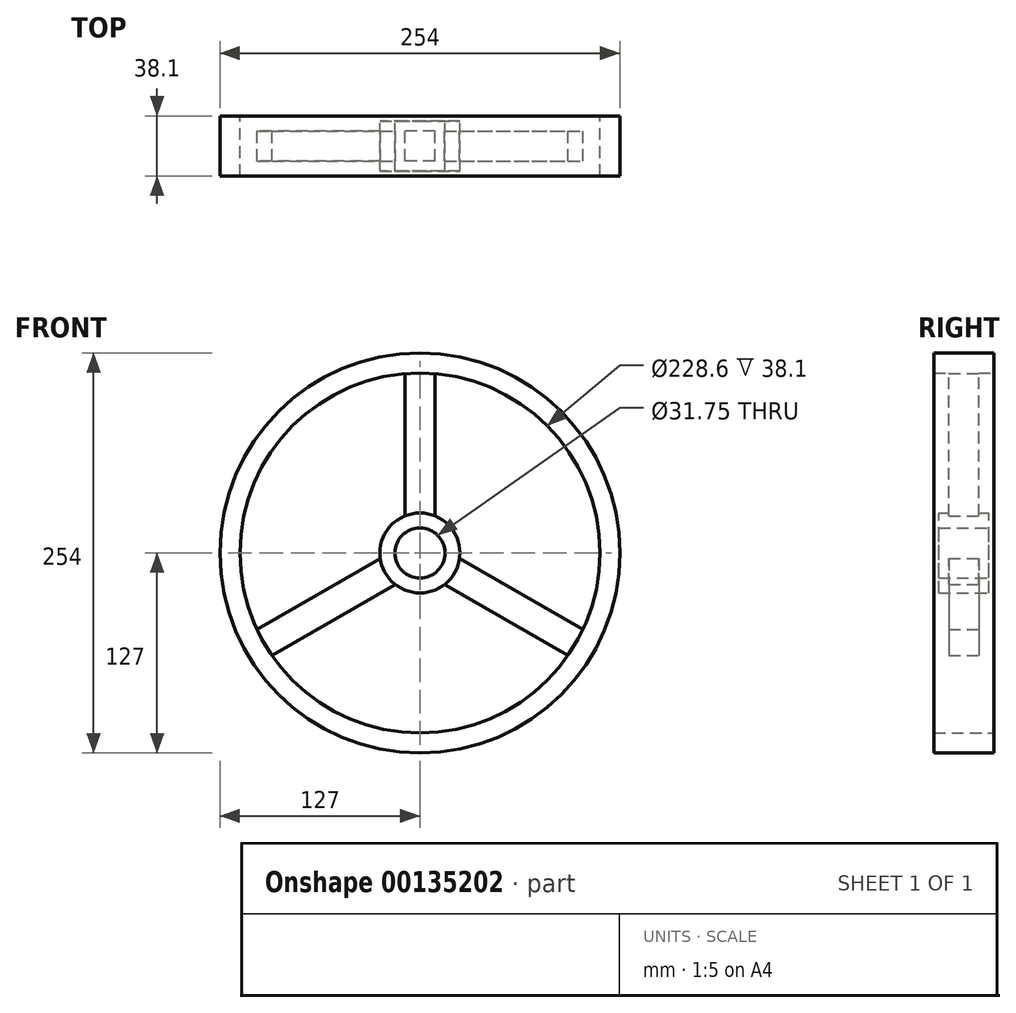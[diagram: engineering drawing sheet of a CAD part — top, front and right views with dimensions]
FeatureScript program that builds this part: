
annotation { "Feature Type Name" : "Feature", "Feature Type Description" : "" }
export const myFeature = defineFeature(function(context is Context, id is Id, definition is map)
    precondition{}
    {
        {
            var Q0;
            Q0=qCreatedBy(makeId("Front.planeOp"),FACE);
            var sketch = newSketch(context, id + "F0", { "sketchPlane" : qUnion([Q0])});
            skCircle(sketch, "E0", {"center": v(0, 0) * mm, "radius": 15.88 * mm});
            skCircle(sketch, "E1", {"center": v(0, 0) * mm, "radius": 25.4 * mm});
            skCircle(sketch, "E2", {"center": v(0, 0) * mm, "radius": 114.3 * mm});
            skCircle(sketch, "E3", {"center": v(0, 0) * mm, "radius": 127 * mm});
            skLineSegment(sketch, "E4", {"start": v(-25.15, -3.52) * mm, "end": v(-103.4, -48.7) * mm});
            skLineSegment(sketch, "E5", {"start": v(15.63, -20.02) * mm, "end": v(93.88, -65.2) * mm});
            skLineSegment(sketch, "E6", {"start": v(25.15, -3.52) * mm, "end": v(103.4, -48.7) * mm});
            skLineSegment(sketch, "E7", {"start": v(-93.88, -65.2) * mm, "end": v(-15.63, -20.02) * mm});
            skLineSegment(sketch, "E8", {"start": v(-9.52, 23.55) * mm, "end": v(-9.53, 113.9) * mm});
            skLineSegment(sketch, "E9", {"start": v(9.53, 23.55) * mm, "end": v(9.52, 113.9) * mm});
            skLineSegment(sketch, "E10", {"start": v(0, 0) * mm, "end": v(-98.99, -57.15) * mm, "construction": true});
            skLineSegment(sketch, "E11", {"start": v(0, 0) * mm, "end": v(98.99, -57.15) * mm, "construction": true});
            skSolve(sketch);
        }
        {
            var Q0;
            Q0 = qSketchRegion(id + "F0", true);
            extrude(context, id + "F1", {"entities" : qUnion([Q0]), "endBound" : BoundingType.SYMMETRIC, "depth" : 38.1 * mm});
        }
        {
            var Q0;
            {var subQ0=sQuery(id+"F0.wireOp",EDGE,"E4");Q0=makeQuery(id+"F0.imprint","IMPRINT",FACE,{"disambiguationData":[TD([[makeQuery(id+"F0.imprint","IMPRINT",EDGE,{"derivedFrom":subQ0}),1.0]])]});}
            var Q1;
            {var subQ0=sQuery(id+"F0.wireOp",EDGE,"E5");Q1=makeQuery(id+"F0.imprint","IMPRINT",FACE,{"disambiguationData":[TD([[makeQuery(id+"F0.imprint","IMPRINT",EDGE,{"derivedFrom":subQ0}),1.0]])]});}
            var Q2;
            {var subQ0=sQuery(id+"F0.wireOp",EDGE,"E8");Q2=makeQuery(id+"F0.imprint","IMPRINT",FACE,{"disambiguationData":[TD([[makeQuery(id+"F0.imprint","IMPRINT",EDGE,{"derivedFrom":subQ0}),-1.0]])]});}
            extrude(context, id + "F2", {"entities" : qUnion([Q0, Q1, Q2]), "operationType" : NewBodyOperationType.ADD, "endBound" : BoundingType.SYMMETRIC, "depth" : 19.05 * mm});
        }
        {
            var Q0;
            Q0=makeQuery(id+"F0.imprint","IMPRINT",FACE,{"disambiguationData":[TD([[makeQuery(id+"F0.imprint","IMPRINT",EDGE,{"derivedFrom":sQuery(id+"F0.wireOp",EDGE,"E0")}),-1.0]])]});
            extrude(context, id + "F3", {"entities" : qUnion([Q0]), "operationType" : NewBodyOperationType.ADD, "endBound" : BoundingType.SYMMETRIC, "depth" : 31.75 * mm});
        }
    });
